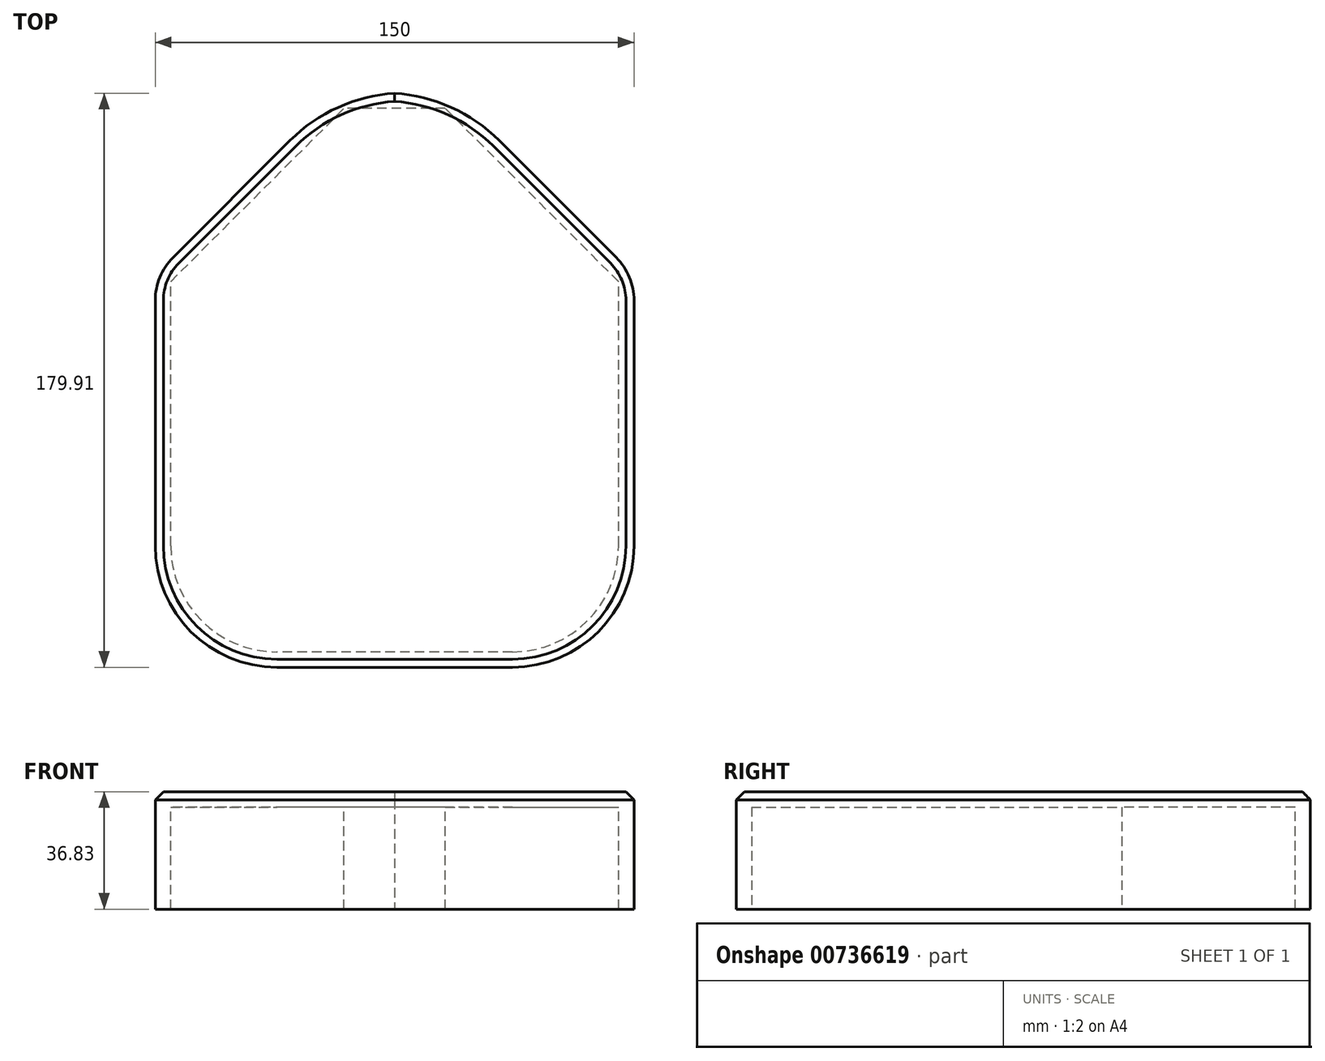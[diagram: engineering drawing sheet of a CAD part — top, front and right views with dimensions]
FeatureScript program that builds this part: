
annotation { "Feature Type Name" : "Feature", "Feature Type Description" : "" }
export const myFeature = defineFeature(function(context is Context, id is Id, definition is map)
    precondition{}
    {
        {
            var Q0;
            Q0=qCreatedBy(makeId("Top.planeOp"),FACE);
            var sketch = newSketch(context, id + "F0", { "sketchPlane" : qUnion([Q0])});
            skLineSegment(sketch, "E0.bottom", {"start": v(0, 0) * mm, "end": v(-150, 0) * mm});
            skLineSegment(sketch, "E0.top", {"start": v(0, 180) * mm, "end": v(-150, 180) * mm});
            skLineSegment(sketch, "E0.left", {"start": v(0, 0) * mm, "end": v(0, 180) * mm});
            skLineSegment(sketch, "E0.right", {"start": v(-150, 0) * mm, "end": v(-150, 180) * mm});
            skSolve(sketch);
        }
        {
            var Q0;
            Q0=makeQuery(id+"F0.imprint","IMPRINT",FACE,{"disambiguationData":[TD([[makeQuery(id+"F0.imprint","IMPRINT",EDGE,{"derivedFrom":sQuery(id+"F0.wireOp",EDGE,"E0.bottom")}),-1.0]])]});
            extrude(context, id + "F1", {"entities" : qUnion([Q0]), "depth" : 36.83 * mm, "offsetDistance" : 25.4 * mm});
        }
        {
            var Q0;
            Q0=makeQuery(id+"F1.opExtrude","SWEPT_EDGE",EDGE,{"disambiguationData":[OSD([sQuery(id+"F0.wireOp",EDGE,"E0.bottom"),sQuery(id+"F0.wireOp",EDGE,"E0.left")])]});
            fillet(context, id + "F2", {"entities" : qUnion([Q0]), "radius" : 38.1 * mm, "allowEdgeOverflow" : false});
        }
        {
            var Q0;
            Q0=makeQuery(id+"F1.opExtrude","SWEPT_EDGE",EDGE,{"disambiguationData":[OSD([sQuery(id+"F0.wireOp",EDGE,"E0.bottom"),sQuery(id+"F0.wireOp",EDGE,"E0.right")])]});
            fillet(context, id + "F3", {"entities" : qUnion([Q0]), "radius" : 38.1 * mm, "tangentPropagation" : true, "allowEdgeOverflow" : false});
        }
        {
            var Q0;
            Q0=makeQuery(id+"F1.opExtrude","SWEPT_EDGE",EDGE,{"disambiguationData":[OSD([sQuery(id+"F0.wireOp",EDGE,"E0.top"),sQuery(id+"F0.wireOp",EDGE,"E0.right")])]});
            chamfer(context, id + "F4", {"entities" : qUnion([Q0]), "width" : 57.15 * mm, "tangentPropagation" : true});
        }
        {
            var Q0;
            Q0=makeQuery(id+"F1.opExtrude","SWEPT_EDGE",EDGE,{"disambiguationData":[OSD([sQuery(id+"F0.wireOp",EDGE,"E0.top"),sQuery(id+"F0.wireOp",EDGE,"E0.left")])]});
            chamfer(context, id + "F5", {"entities" : qUnion([Q0]), "width" : 57.15 * mm, "tangentPropagation" : true});
        }
        {
            var Q0;
            Q0=makeQuery(id+"F1.opExtrude","CAP_FACE",FACE,{"disambiguationData":[OSD([sQuery(id+"F0.wireOp",EDGE,"E0.bottom"),sQuery(id+"F0.wireOp",EDGE,"E0.top"),sQuery(id+"F0.wireOp",EDGE,"E0.left"),sQuery(id+"F0.wireOp",EDGE,"E0.right")])],"isStart":true});
            shell(context, id + "F6", {"entities" : qUnion([Q0]), "thickness" : 4.83 * mm});
        }
        {
            var Q0;
            {var subQ0=sQuery(id+"F0.wireOp",EDGE,"E0.top");Q0=makeQuery(id+"F4.opChamfer","BLEND_EDGE",EDGE,{"blendedFrom":[makeQuery(id+"F1.opExtrude","SWEPT_EDGE",EDGE,{"disambiguationData":[OSD([subQ0,sQuery(id+"F0.wireOp",EDGE,"E0.right")])]}),makeQuery(id+"F1.opExtrude","SWEPT_FACE",FACE,{"disambiguationData":[OSD([subQ0])]})],"blendedInto":[makeQuery(id+"F1.opExtrude","SWEPT_FACE",FACE,{"disambiguationData":[OSD([subQ0])]})]});}
            var Q1;
            {var subQ0=sQuery(id+"F0.wireOp",EDGE,"E0.top");Q1=makeQuery(id+"F5.opChamfer","BLEND_EDGE",EDGE,{"blendedFrom":[makeQuery(id+"F1.opExtrude","SWEPT_EDGE",EDGE,{"disambiguationData":[OSD([subQ0,sQuery(id+"F0.wireOp",EDGE,"E0.left")])]}),makeQuery(id+"F1.opExtrude","SWEPT_FACE",FACE,{"disambiguationData":[OSD([subQ0])]})],"blendedInto":[makeQuery(id+"F1.opExtrude","SWEPT_FACE",FACE,{"disambiguationData":[OSD([subQ0])]})]});}
            fillet(context, id + "F7", {"entities" : qUnion([Q0, Q1]), "radius" : 50.8 * mm, "tangentPropagation" : true, "allowEdgeOverflow" : false});
        }
        {
            var Q0;
            {var subQ0=sQuery(id+"F0.wireOp",EDGE,"E0.right");Q0=makeQuery(id+"F4.opChamfer","BLEND_EDGE",EDGE,{"blendedFrom":[makeQuery(id+"F1.opExtrude","SWEPT_EDGE",EDGE,{"disambiguationData":[OSD([sQuery(id+"F0.wireOp",EDGE,"E0.top"),subQ0])]}),makeQuery(id+"F1.opExtrude","SWEPT_FACE",FACE,{"disambiguationData":[OSD([subQ0])]})],"blendedInto":[makeQuery(id+"F1.opExtrude","SWEPT_FACE",FACE,{"disambiguationData":[OSD([subQ0])]})]});}
            var Q1;
            {var subQ0=sQuery(id+"F0.wireOp",EDGE,"E0.left");Q1=makeQuery(id+"F5.opChamfer","BLEND_EDGE",EDGE,{"blendedFrom":[makeQuery(id+"F1.opExtrude","SWEPT_EDGE",EDGE,{"disambiguationData":[OSD([sQuery(id+"F0.wireOp",EDGE,"E0.top"),subQ0])]}),makeQuery(id+"F1.opExtrude","SWEPT_FACE",FACE,{"disambiguationData":[OSD([subQ0])]})],"blendedInto":[makeQuery(id+"F1.opExtrude","SWEPT_FACE",FACE,{"disambiguationData":[OSD([subQ0])]})]});}
            fillet(context, id + "F8", {"entities" : qUnion([Q0, Q1]), "radius" : 19.05 * mm, "tangentPropagation" : true, "allowEdgeOverflow" : false});
        }
        {
            var Q0;
            {var subQ0=sQuery(id+"F0.wireOp",EDGE,"E0.left");var subQ1=sQuery(id+"F0.wireOp",EDGE,"E0.top");Q0=makeQuery(id+"F7.opFillet","BLEND_EDGE",EDGE,{"blendedFrom":[makeQuery(id+"F5.opChamfer","BLEND_EDGE",EDGE,{"blendedFrom":[makeQuery(id+"F1.opExtrude","SWEPT_EDGE",EDGE,{"disambiguationData":[OSD([subQ1,subQ0])]}),makeQuery(id+"F1.opExtrude","SWEPT_FACE",FACE,{"disambiguationData":[OSD([subQ1])]})],"blendedInto":[makeQuery(id+"F1.opExtrude","SWEPT_FACE",FACE,{"disambiguationData":[OSD([subQ1])]})]}),makeQuery(id+"F1.opExtrude","CAP_FACE",FACE,{"disambiguationData":[OSD([sQuery(id+"F0.wireOp",EDGE,"E0.bottom"),subQ1,subQ0,sQuery(id+"F0.wireOp",EDGE,"E0.right")])],"isStart":false})],"blendedInto":[makeQuery(id+"F1.opExtrude","CAP_FACE",FACE,{"disambiguationData":[OSD([sQuery(id+"F0.wireOp",EDGE,"E0.bottom"),subQ1,subQ0,sQuery(id+"F0.wireOp",EDGE,"E0.right")])],"isStart":false})]});}
            var Q1;
            {var subQ0=sQuery(id+"F0.wireOp",EDGE,"E0.right");var subQ1=sQuery(id+"F0.wireOp",EDGE,"E0.top");Q1=makeQuery(id+"F7.opFillet","BLEND_EDGE",EDGE,{"blendedFrom":[makeQuery(id+"F4.opChamfer","BLEND_EDGE",EDGE,{"blendedFrom":[makeQuery(id+"F1.opExtrude","SWEPT_EDGE",EDGE,{"disambiguationData":[OSD([subQ1,subQ0])]}),makeQuery(id+"F1.opExtrude","SWEPT_FACE",FACE,{"disambiguationData":[OSD([subQ1])]})],"blendedInto":[makeQuery(id+"F1.opExtrude","SWEPT_FACE",FACE,{"disambiguationData":[OSD([subQ1])]})]}),makeQuery(id+"F1.opExtrude","CAP_FACE",FACE,{"disambiguationData":[OSD([sQuery(id+"F0.wireOp",EDGE,"E0.bottom"),subQ1,sQuery(id+"F0.wireOp",EDGE,"E0.left"),subQ0])],"isStart":false})],"blendedInto":[makeQuery(id+"F1.opExtrude","CAP_FACE",FACE,{"disambiguationData":[OSD([sQuery(id+"F0.wireOp",EDGE,"E0.bottom"),subQ1,sQuery(id+"F0.wireOp",EDGE,"E0.left"),subQ0])],"isStart":false})]});}
            var Q2;
            {var subQ0=sQuery(id+"F0.wireOp",EDGE,"E0.right");var subQ1=sQuery(id+"F0.wireOp",EDGE,"E0.top");Q2=makeQuery(id+"F4.opChamfer","BLEND_EDGE",EDGE,{"blendedFrom":[makeQuery(id+"F1.opExtrude","SWEPT_EDGE",EDGE,{"disambiguationData":[OSD([subQ1,subQ0])]}),makeQuery(id+"F1.opExtrude","CAP_FACE",FACE,{"disambiguationData":[OSD([sQuery(id+"F0.wireOp",EDGE,"E0.bottom"),subQ1,sQuery(id+"F0.wireOp",EDGE,"E0.left"),subQ0])],"isStart":false})],"blendedInto":[makeQuery(id+"F1.opExtrude","CAP_FACE",FACE,{"disambiguationData":[OSD([sQuery(id+"F0.wireOp",EDGE,"E0.bottom"),subQ1,sQuery(id+"F0.wireOp",EDGE,"E0.left"),subQ0])],"isStart":false})]});}
            var Q3;
            Q3=makeQuery(id+"F1.opExtrude","CAP_EDGE",EDGE,{"disambiguationData":[OSD([sQuery(id+"F0.wireOp",EDGE,"E0.right")])],"isStart":false});
            var Q4;
            {var subQ0=sQuery(id+"F0.wireOp",EDGE,"E0.right");var subQ1=sQuery(id+"F0.wireOp",EDGE,"E0.top");Q4=makeQuery(id+"F8.opFillet","BLEND_EDGE",EDGE,{"blendedFrom":[makeQuery(id+"F4.opChamfer","BLEND_EDGE",EDGE,{"blendedFrom":[makeQuery(id+"F1.opExtrude","SWEPT_EDGE",EDGE,{"disambiguationData":[OSD([subQ1,subQ0])]}),makeQuery(id+"F1.opExtrude","SWEPT_FACE",FACE,{"disambiguationData":[OSD([subQ0])]})],"blendedInto":[makeQuery(id+"F1.opExtrude","SWEPT_FACE",FACE,{"disambiguationData":[OSD([subQ0])]})]}),makeQuery(id+"F1.opExtrude","CAP_FACE",FACE,{"disambiguationData":[OSD([sQuery(id+"F0.wireOp",EDGE,"E0.bottom"),subQ1,sQuery(id+"F0.wireOp",EDGE,"E0.left"),subQ0])],"isStart":false})],"blendedInto":[makeQuery(id+"F1.opExtrude","CAP_FACE",FACE,{"disambiguationData":[OSD([sQuery(id+"F0.wireOp",EDGE,"E0.bottom"),subQ1,sQuery(id+"F0.wireOp",EDGE,"E0.left"),subQ0])],"isStart":false})]});}
            var Q5;
            {var subQ0=sQuery(id+"F0.wireOp",EDGE,"E0.right");var subQ1=sQuery(id+"F0.wireOp",EDGE,"E0.bottom");Q5=makeQuery(id+"F3.opFillet","BLEND_EDGE",EDGE,{"blendedFrom":[makeQuery(id+"F1.opExtrude","SWEPT_EDGE",EDGE,{"disambiguationData":[OSD([subQ1,subQ0])]}),makeQuery(id+"F1.opExtrude","CAP_FACE",FACE,{"disambiguationData":[OSD([subQ1,sQuery(id+"F0.wireOp",EDGE,"E0.top"),sQuery(id+"F0.wireOp",EDGE,"E0.left"),subQ0])],"isStart":false})],"blendedInto":[makeQuery(id+"F1.opExtrude","CAP_FACE",FACE,{"disambiguationData":[OSD([subQ1,sQuery(id+"F0.wireOp",EDGE,"E0.top"),sQuery(id+"F0.wireOp",EDGE,"E0.left"),subQ0])],"isStart":false})]});}
            var Q6;
            Q6=makeQuery(id+"F1.opExtrude","CAP_EDGE",EDGE,{"disambiguationData":[OSD([sQuery(id+"F0.wireOp",EDGE,"E0.bottom")])],"isStart":false});
            var Q7;
            {var subQ0=sQuery(id+"F0.wireOp",EDGE,"E0.left");var subQ1=sQuery(id+"F0.wireOp",EDGE,"E0.bottom");Q7=makeQuery(id+"F2.opFillet","BLEND_EDGE",EDGE,{"blendedFrom":[makeQuery(id+"F1.opExtrude","SWEPT_EDGE",EDGE,{"disambiguationData":[OSD([subQ1,subQ0])]}),makeQuery(id+"F1.opExtrude","CAP_FACE",FACE,{"disambiguationData":[OSD([subQ1,sQuery(id+"F0.wireOp",EDGE,"E0.top"),subQ0,sQuery(id+"F0.wireOp",EDGE,"E0.right")])],"isStart":false})],"blendedInto":[makeQuery(id+"F1.opExtrude","CAP_FACE",FACE,{"disambiguationData":[OSD([subQ1,sQuery(id+"F0.wireOp",EDGE,"E0.top"),subQ0,sQuery(id+"F0.wireOp",EDGE,"E0.right")])],"isStart":false})]});}
            var Q8;
            Q8=makeQuery(id+"F1.opExtrude","CAP_EDGE",EDGE,{"disambiguationData":[OSD([sQuery(id+"F0.wireOp",EDGE,"E0.left")])],"isStart":false});
            var Q9;
            {var subQ0=sQuery(id+"F0.wireOp",EDGE,"E0.left");var subQ1=sQuery(id+"F0.wireOp",EDGE,"E0.top");Q9=makeQuery(id+"F8.opFillet","BLEND_EDGE",EDGE,{"blendedFrom":[makeQuery(id+"F5.opChamfer","BLEND_EDGE",EDGE,{"blendedFrom":[makeQuery(id+"F1.opExtrude","SWEPT_EDGE",EDGE,{"disambiguationData":[OSD([subQ1,subQ0])]}),makeQuery(id+"F1.opExtrude","SWEPT_FACE",FACE,{"disambiguationData":[OSD([subQ0])]})],"blendedInto":[makeQuery(id+"F1.opExtrude","SWEPT_FACE",FACE,{"disambiguationData":[OSD([subQ0])]})]}),makeQuery(id+"F1.opExtrude","CAP_FACE",FACE,{"disambiguationData":[OSD([sQuery(id+"F0.wireOp",EDGE,"E0.bottom"),subQ1,subQ0,sQuery(id+"F0.wireOp",EDGE,"E0.right")])],"isStart":false})],"blendedInto":[makeQuery(id+"F1.opExtrude","CAP_FACE",FACE,{"disambiguationData":[OSD([sQuery(id+"F0.wireOp",EDGE,"E0.bottom"),subQ1,subQ0,sQuery(id+"F0.wireOp",EDGE,"E0.right")])],"isStart":false})]});}
            chamfer(context, id + "F9", {"entities" : qUnion([Q0, Q1, Q2, Q3, Q4, Q5, Q6, Q7, Q8, Q9]), "width" : 2.54 * mm, "tangentPropagation" : true});
        }
    });
